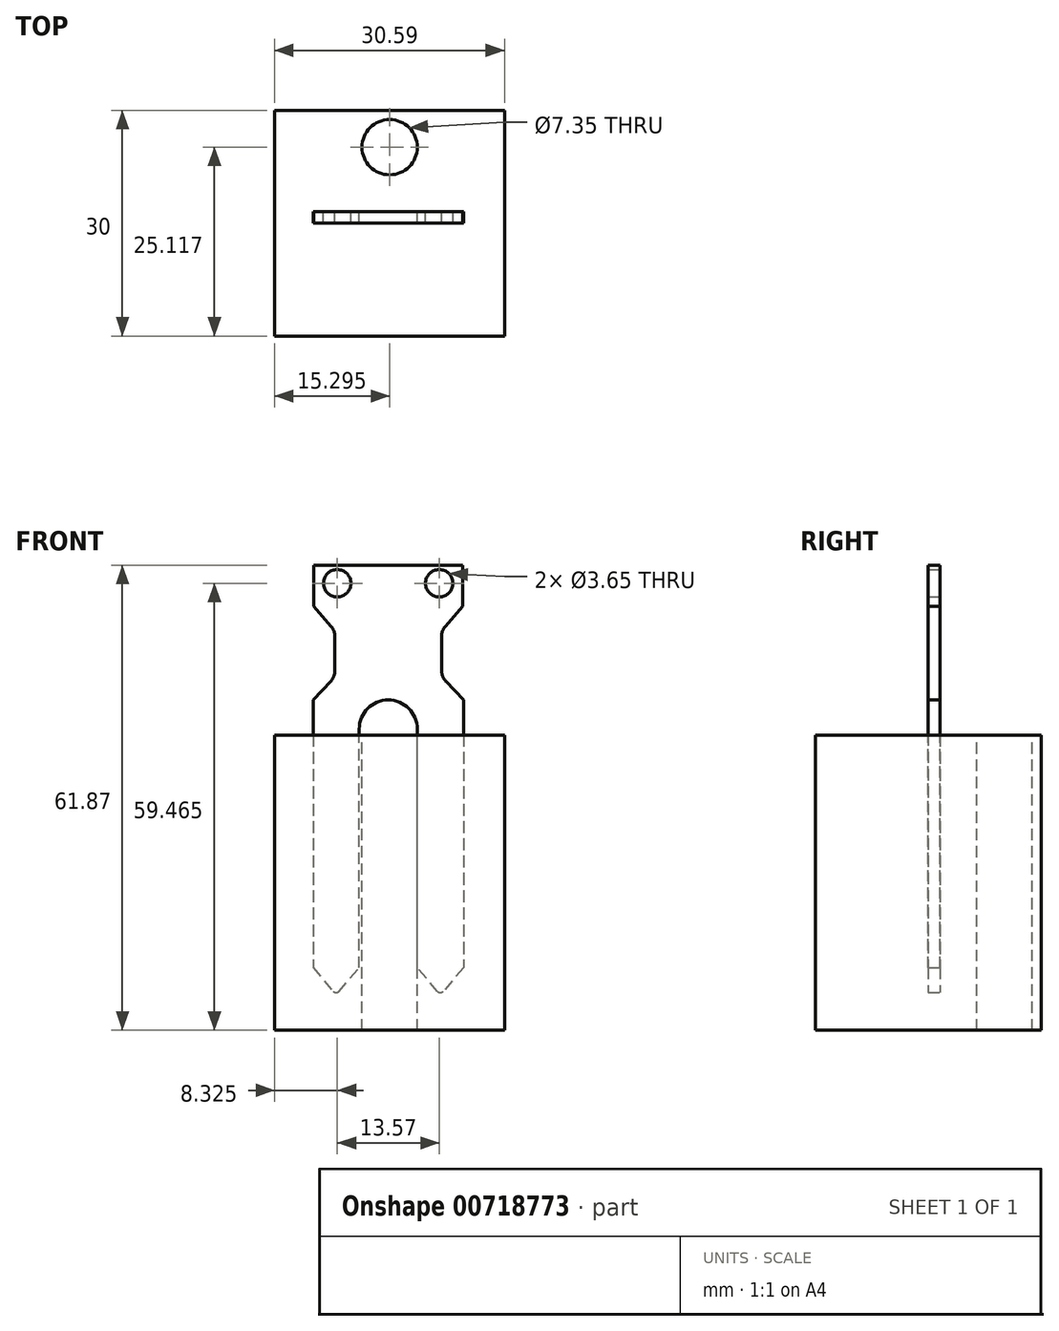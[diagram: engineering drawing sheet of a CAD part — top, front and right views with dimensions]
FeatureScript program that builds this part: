
annotation { "Feature Type Name" : "Feature", "Feature Type Description" : "" }
export const myFeature = defineFeature(function(context is Context, id is Id, definition is map)
    precondition{}
    {
        {
            var Q0;
            Q0=qCreatedBy(makeId("Front.planeOp"),FACE);
            var sketch = newSketch(context, id + "F0", { "sketchPlane" : qUnion([Q0])});
            skLineSegment(sketch, "E0", {"start": v(0, 0) * mm, "end": v(19.76, 0) * mm});
            skLineSegment(sketch, "E1", {"start": v(19.76, 0) * mm, "end": v(19.76, -5.5) * mm});
            skLineSegment(sketch, "E2", {"start": v(19.76, -5.5) * mm, "end": v(16.99, -8.68) * mm});
            skLineSegment(sketch, "E3", {"start": v(16.99, -8.68) * mm, "end": v(16.99, -14.86) * mm});
            skLineSegment(sketch, "E4", {"start": v(16.99, -14.86) * mm, "end": v(19.88, -17.93) * mm});
            skLineSegment(sketch, "E5", {"start": v(19.88, -17.93) * mm, "end": v(19.88, -53.56) * mm});
            skLineSegment(sketch, "E6", {"start": v(19.88, -53.56) * mm, "end": v(16.81, -57.14) * mm});
            skLineSegment(sketch, "E7", {"start": v(16.81, -57.14) * mm, "end": v(13.74, -53.56) * mm});
            skLineSegment(sketch, "E8", {"start": v(9.88, 0) * mm, "end": v(9.88, -60.7) * mm, "construction": true});
            skLineSegment(sketch, "E9", {"start": v(13.74, -53.56) * mm, "end": v(13.74, -21.79) * mm});
            skLineSegment(sketch, "E10.MirrorCS", {"start": v(0, 0) * mm, "end": v(0, -5.5) * mm});
            skLineSegment(sketch, "E11.MirrorCS", {"start": v(0, -5.5) * mm, "end": v(2.78, -8.68) * mm});
            skLineSegment(sketch, "E12.MirrorCS", {"start": v(2.78, -8.68) * mm, "end": v(2.78, -14.86) * mm});
            skLineSegment(sketch, "E13.MirrorCS", {"start": v(2.78, -14.86) * mm, "end": v(-0.12, -17.93) * mm});
            skLineSegment(sketch, "E14.MirrorCS", {"start": v(-0.12, -17.93) * mm, "end": v(-0.12, -53.56) * mm});
            skLineSegment(sketch, "E15.MirrorCS", {"start": v(-0.12, -53.56) * mm, "end": v(2.95, -57.14) * mm});
            skLineSegment(sketch, "E16.MirrorCS", {"start": v(2.95, -57.14) * mm, "end": v(6.02, -53.56) * mm});
            skLineSegment(sketch, "E17.MirrorCS", {"start": v(6.02, -53.56) * mm, "end": v(6.02, -21.79) * mm});
            skArc(sketch, "E18", {"start": v(6.02, -21.79) * mm, "mid": v(9.88, -17.93) * mm, "end": v(13.74, -21.79) * mm});
            skPoint(sketch, "E19", {"position": v(9.88, -17.93) * mm});
            skCircle(sketch, "E20", {"center": v(16.67, -2.4) * mm, "radius": 1.82 * mm});
            skCircle(sketch, "E21.MirrorC", {"center": v(3.1, -2.4) * mm, "radius": 1.82 * mm});
            skSolve(sketch);
        }
        {
            var Q0;
            Q0 = qSketchRegion(id + "F0", true);
            extrude(context, id + "F1", {"entities" : qUnion([Q0]), "depth" : 1.56 * mm, "offsetDistance" : 25 * mm});
        }
        {
            var Q0;
            Q0=makeQuery(id+"F1.opExtrude","SWEPT_EDGE",EDGE,{"disambiguationData":[OSD([sQuery(id+"F0.wireOp",EDGE,"E11.MirrorCS"),sQuery(id+"F0.wireOp",EDGE,"E12.MirrorCS")])]});
            var Q1;
            Q1=makeQuery(id+"F1.opExtrude","SWEPT_EDGE",EDGE,{"disambiguationData":[OSD([sQuery(id+"F0.wireOp",EDGE,"E12.MirrorCS"),sQuery(id+"F0.wireOp",EDGE,"E13.MirrorCS")])]});
            var Q2;
            Q2=makeQuery(id+"F1.opExtrude","SWEPT_EDGE",EDGE,{"disambiguationData":[OSD([sQuery(id+"F0.wireOp",EDGE,"E2"),sQuery(id+"F0.wireOp",EDGE,"E3")])]});
            var Q3;
            Q3=makeQuery(id+"F1.opExtrude","SWEPT_EDGE",EDGE,{"disambiguationData":[OSD([sQuery(id+"F0.wireOp",EDGE,"E3"),sQuery(id+"F0.wireOp",EDGE,"E4")])]});
            fillet(context, id + "F2", {"entities" : qUnion([Q0, Q1, Q2, Q3]), "radius" : 2 * mm, "tangentPropagation" : true, "allowEdgeOverflow" : false});
        }
        {
            var Q0;
            Q0=makeQuery(id+"F1.opExtrude","SWEPT_EDGE",EDGE,{"disambiguationData":[OSD([sQuery(id+"F0.wireOp",EDGE,"E15.MirrorCS"),sQuery(id+"F0.wireOp",EDGE,"E16.MirrorCS")])]});
            var Q1;
            Q1=makeQuery(id+"F1.opExtrude","SWEPT_EDGE",EDGE,{"disambiguationData":[OSD([sQuery(id+"F0.wireOp",EDGE,"E6"),sQuery(id+"F0.wireOp",EDGE,"E7")])]});
            fillet(context, id + "F3", {"entities" : qUnion([Q0, Q1]), "radius" : .5 * mm, "tangentPropagation" : true, "allowEdgeOverflow" : false});
        }
        {
            var Q0;
            Q0=makeQuery(id+"F1.opExtrude","CAP_FACE",FACE,{"disambiguationData":[OSD([sQuery(id+"F0.wireOp",EDGE,"E0"),sQuery(id+"F0.wireOp",EDGE,"E1"),sQuery(id+"F0.wireOp",EDGE,"E2"),sQuery(id+"F0.wireOp",EDGE,"E3"),sQuery(id+"F0.wireOp",EDGE,"E4"),sQuery(id+"F0.wireOp",EDGE,"E5"),sQuery(id+"F0.wireOp",EDGE,"E6"),sQuery(id+"F0.wireOp",EDGE,"E7"),sQuery(id+"F0.wireOp",EDGE,"E9"),sQuery(id+"F0.wireOp",EDGE,"E10.MirrorCS"),sQuery(id+"F0.wireOp",EDGE,"E11.MirrorCS"),sQuery(id+"F0.wireOp",EDGE,"E12.MirrorCS"),sQuery(id+"F0.wireOp",EDGE,"E13.MirrorCS"),sQuery(id+"F0.wireOp",EDGE,"E14.MirrorCS"),sQuery(id+"F0.wireOp",EDGE,"E15.MirrorCS"),sQuery(id+"F0.wireOp",EDGE,"E16.MirrorCS"),sQuery(id+"F0.wireOp",EDGE,"E17.MirrorCS"),sQuery(id+"F0.wireOp",EDGE,"E18"),sQuery(id+"F0.wireOp",EDGE,"E20"),sQuery(id+"F0.wireOp",EDGE,"E21.MirrorC")])],"isStart":false});
            var sketch = newSketch(context, id + "F4", { "sketchPlane" : qUnion([Q0])});
            skLineSegment(sketch, "E22.bottom", {"start": v(-5.23, -22.64) * mm, "end": v(25.36, -22.64) * mm});
            skLineSegment(sketch, "E22.top", {"start": v(-5.23, -61.87) * mm, "end": v(25.36, -61.87) * mm});
            skLineSegment(sketch, "E22.left", {"start": v(-5.23, -22.64) * mm, "end": v(-5.23, -61.87) * mm});
            skLineSegment(sketch, "E22.right", {"start": v(25.36, -22.64) * mm, "end": v(25.36, -61.87) * mm});
            skSolve(sketch);
        }
        {
            var Q0;
            Q0 = qSketchRegion(id + "F4", true);
            extrude(context, id + "F5", {"entities" : qUnion([Q0]), "oppositeDirection" : true, "depth" : 15 * mm, "offsetDistance" : 25 * mm, "hasSecondDirection" : true, "secondDirectionOppositeDirection" : false, "secondDirectionDepth" : 15 * mm});
        }
        {
            var Q0;
            Q0=makeQuery(id+"F1.opExtrude","SWEPT_BODY",BODY,{"disambiguationData":[OSD([sQuery(id+"F0.wireOp",EDGE,"E0"),sQuery(id+"F0.wireOp",EDGE,"E1"),sQuery(id+"F0.wireOp",EDGE,"E2"),sQuery(id+"F0.wireOp",EDGE,"E3"),sQuery(id+"F0.wireOp",EDGE,"E4"),sQuery(id+"F0.wireOp",EDGE,"E5"),sQuery(id+"F0.wireOp",EDGE,"E6"),sQuery(id+"F0.wireOp",EDGE,"E7"),sQuery(id+"F0.wireOp",EDGE,"E9"),sQuery(id+"F0.wireOp",EDGE,"E10.MirrorCS"),sQuery(id+"F0.wireOp",EDGE,"E11.MirrorCS"),sQuery(id+"F0.wireOp",EDGE,"E12.MirrorCS"),sQuery(id+"F0.wireOp",EDGE,"E13.MirrorCS"),sQuery(id+"F0.wireOp",EDGE,"E14.MirrorCS"),sQuery(id+"F0.wireOp",EDGE,"E15.MirrorCS"),sQuery(id+"F0.wireOp",EDGE,"E16.MirrorCS"),sQuery(id+"F0.wireOp",EDGE,"E17.MirrorCS"),sQuery(id+"F0.wireOp",EDGE,"E18"),sQuery(id+"F0.wireOp",EDGE,"E20"),sQuery(id+"F0.wireOp",EDGE,"E21.MirrorC")])]});
            var Q1;
            Q1=makeQuery(id+"F5.opExtrude","SWEPT_BODY",BODY,{"disambiguationData":[OSD([sQuery(id+"F4.wireOp",EDGE,"E22.bottom"),sQuery(id+"F4.wireOp",EDGE,"E22.top"),sQuery(id+"F4.wireOp",EDGE,"E22.left"),sQuery(id+"F4.wireOp",EDGE,"E22.right")])]});
            booleanBodies(context, id + "F6", {"operationType" : BooleanOperationType.SUBTRACTION, "tools" : qUnion([Q0]), "targets" : qUnion([Q1]), "keepTools" : true});
        }
        {
            var Q0;
            Q0=makeQuery(id+"F5.opExtrude","SWEPT_FACE",FACE,{"disambiguationData":[OSD([sQuery(id+"F4.wireOp",EDGE,"E22.bottom")])]});
            var sketch = newSketch(context, id + "F7", { "sketchPlane" : qUnion([Q0])});
            skCircle(sketch, "E23", {"center": v(10.07, 8.56) * mm, "radius": 3.67 * mm});
            skPoint(sketch, "E23.centerSnap0", {"position": v(10.07, 13.44) * mm});
            skSolve(sketch);
        }
        {
            var Q0;
            Q0=makeQuery(id+"F7.imprint","IMPRINT",FACE,{"disambiguationData":[TD([[makeQuery(id+"F7.imprint","IMPRINT",EDGE,{"derivedFrom":sQuery(id+"F7.wireOp",EDGE,"E23")}),1.0]])]});
            extrude(context, id + "F8", {"entities" : qUnion([Q0]), "operationType" : NewBodyOperationType.REMOVE, "oppositeDirection" : true, "depth" : 54.4 * mm, "offsetDistance" : 25 * mm});
        }
    });
